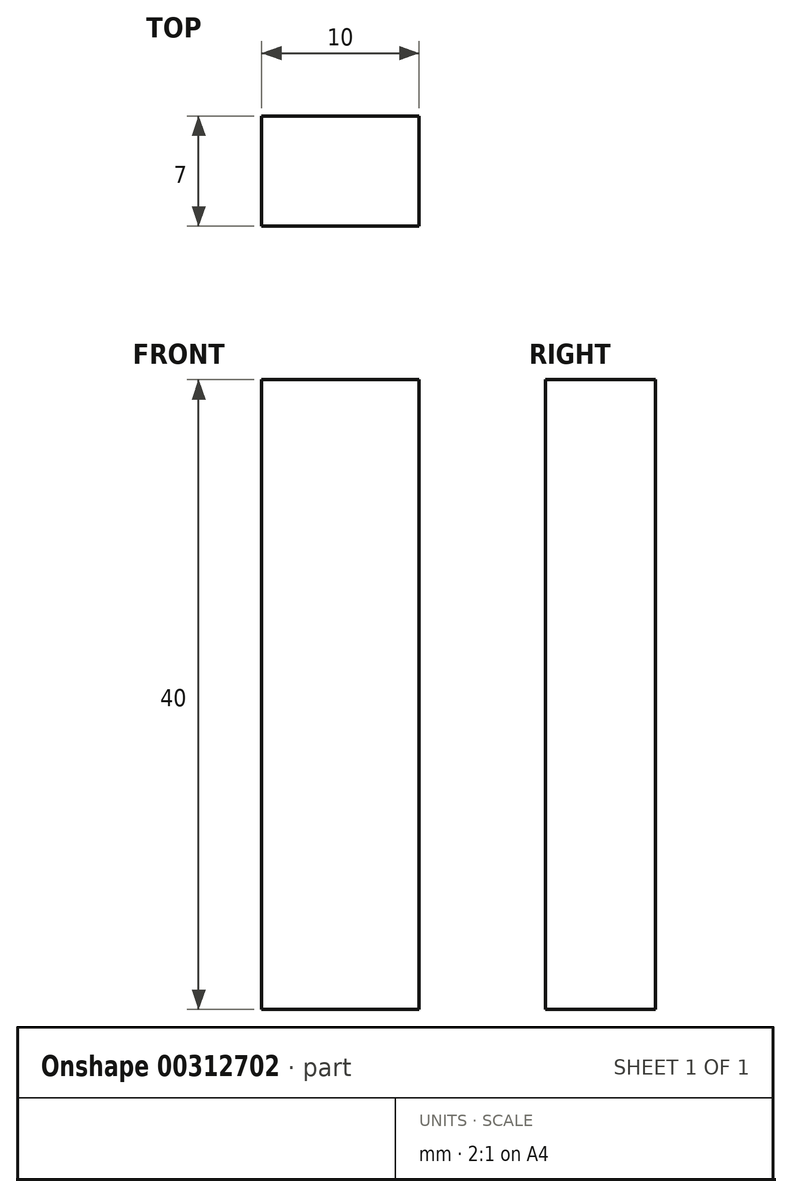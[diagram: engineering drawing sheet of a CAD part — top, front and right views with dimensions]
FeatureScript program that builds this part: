
annotation { "Feature Type Name" : "Feature", "Feature Type Description" : "" }
export const myFeature = defineFeature(function(context is Context, id is Id, definition is map)
    precondition{}
    {
        {
            var Q0;
            Q0=qCreatedBy(makeId("Top.planeOp"),FACE);
            var sketch = newSketch(context, id + "F0", { "sketchPlane" : qUnion([Q0])});
            skLineSegment(sketch, "E0.bottom", {"start": v(21.08, -22.94) * mm, "end": v(31.08, -22.94) * mm});
            skLineSegment(sketch, "E0.top", {"start": v(21.08, -29.94) * mm, "end": v(31.08, -29.94) * mm});
            skLineSegment(sketch, "E0.left", {"start": v(21.08, -22.94) * mm, "end": v(21.08, -29.94) * mm});
            skLineSegment(sketch, "E0.right", {"start": v(31.08, -22.94) * mm, "end": v(31.08, -29.94) * mm});
            skSolve(sketch);
        }
        {
            var Q0;
            Q0=makeQuery(id+"F0.imprint","IMPRINT",FACE,{"disambiguationData":[TD([[makeQuery(id+"F0.imprint","IMPRINT",EDGE,{"derivedFrom":sQuery(id+"F0.wireOp",EDGE,"E0.bottom")}),-1.0]])]});
            extrude(context, id + "F1", {"entities" : qUnion([Q0]), "depth" : 40 * mm});
        }
    });
